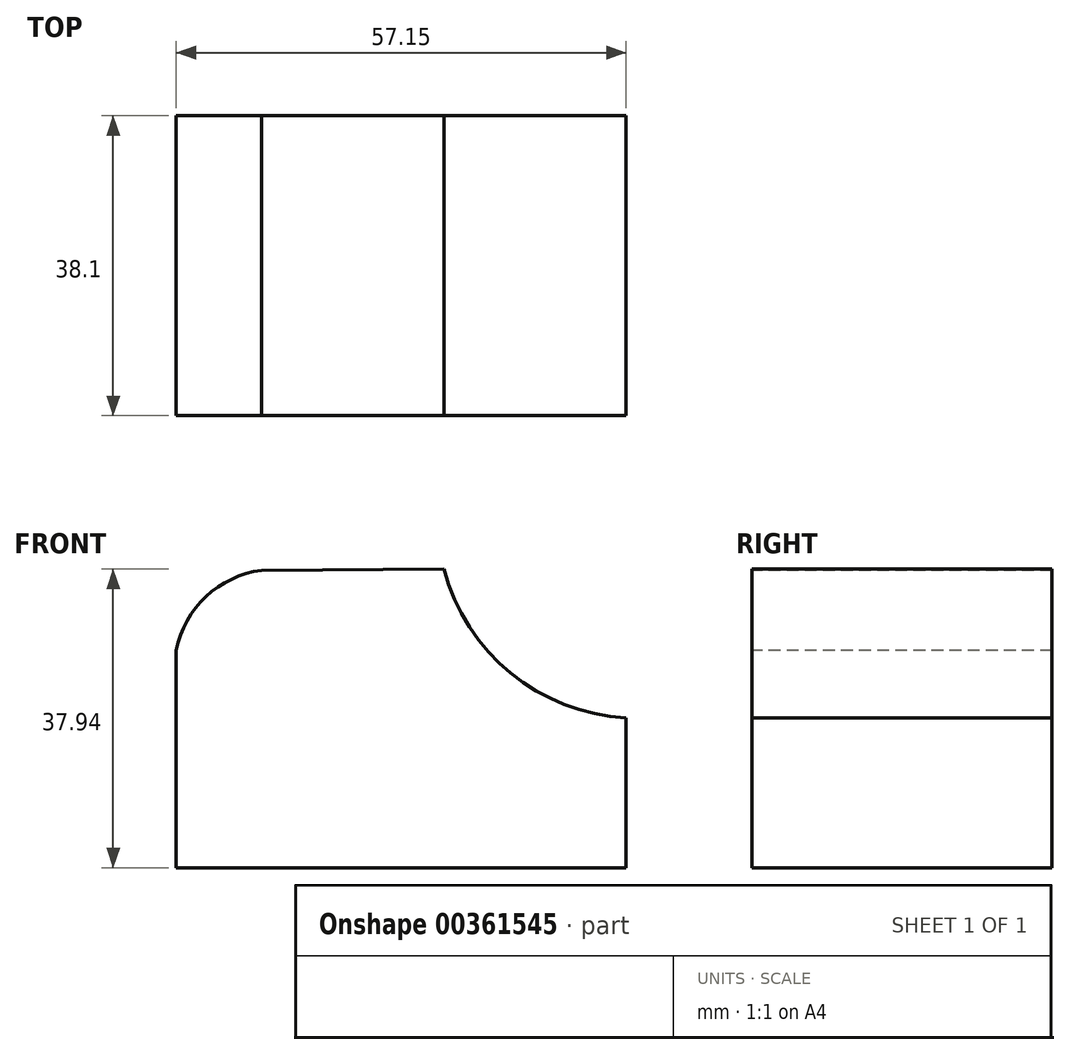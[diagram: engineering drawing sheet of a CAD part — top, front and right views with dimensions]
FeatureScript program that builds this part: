
annotation { "Feature Type Name" : "Feature", "Feature Type Description" : "" }
export const myFeature = defineFeature(function(context is Context, id is Id, definition is map)
    precondition{}
    {
        {
            var Q0;
            Q0=qCreatedBy(makeId("Front.planeOp"),FACE);
            var sketch = newSketch(context, id + "F0", { "sketchPlane" : qUnion([Q0])});
            skLineSegment(sketch, "E0", {"start": v(0, 37.71) * mm, "end": v(0, 0) * mm});
            skLineSegment(sketch, "E1", {"start": v(0, 0) * mm, "end": v(57.15, 0) * mm});
            skLineSegment(sketch, "E2", {"start": v(57.15, 0) * mm, "end": v(57.15, 38.1) * mm});
            skLineSegment(sketch, "E3", {"start": v(57.15, 38.1) * mm, "end": v(0, 37.71) * mm});
            skSolve(sketch);
        }
        {
            var Q0;
            Q0 = qSketchRegion(id + "F0", true);
            extrude(context, id + "F1", {"entities" : qUnion([Q0]), "depth" : 38.1 * mm});
        }
        {
            var Q0;
            Q0=makeQuery(id+"F1.opExtrude","CAP_FACE",FACE,{"disambiguationData":[OSD([sQuery(id+"F0.wireOp",EDGE,"E0"),sQuery(id+"F0.wireOp",EDGE,"E1"),sQuery(id+"F0.wireOp",EDGE,"E2"),sQuery(id+"F0.wireOp",EDGE,"E3")])],"isStart":false});
            var sketch = newSketch(context, id + "F2", { "sketchPlane" : qUnion([Q0])});
            skArc(sketch, "E4", {"start": v(10.83, 37.78) * mm, "mid": v(2.16, 32.61) * mm, "end": v(0, 22.75) * mm});
            skSolve(sketch);
        }
        {
            var Q0;
            {var subQ0=sQuery(id+"F2.wireOp",EDGE,"E4");var subQ1=makeQuery(id+"F1.opExtrude","CAP_EDGE",EDGE,{"disambiguationData":[OSD([sQuery(id+"F0.wireOp",EDGE,"E3")])],"isStart":false});var subQ2=makeQuery(id+"F2.imprint","INTERSECT",VERTEX,{"derivedFrom":[subQ1,subQ0]});Q0=makeQuery(id+"F2.imprint","IMPRINT",FACE,{"disambiguationData":[TD([[makeQuery(id+"F2.imprint","IMPRINT",EDGE,{"disambiguationData":[TD([[subQ2,-1.0]])],"derivedFrom":subQ0}),-1.0]])]});}
            extrude(context, id + "F3", {"entities" : qUnion([Q0]), "operationType" : NewBodyOperationType.REMOVE, "oppositeDirection" : true, "depth" : 38.1 * mm});
        }
        {
            var Q0;
            Q0=makeQuery(id+"F1.opExtrude","CAP_FACE",FACE,{"disambiguationData":[OSD([sQuery(id+"F0.wireOp",EDGE,"E0"),sQuery(id+"F0.wireOp",EDGE,"E1"),sQuery(id+"F0.wireOp",EDGE,"E2"),sQuery(id+"F0.wireOp",EDGE,"E3")])],"isStart":false});
            var sketch = newSketch(context, id + "F4", { "sketchPlane" : qUnion([Q0])});
            skArc(sketch, "E5", {"start": v(34, 37.94) * mm, "mid": v(42.5, 24.73) * mm, "end": v(57.15, 19.05) * mm});
            skSolve(sketch);
        }
        {
            var Q0;
            {var subQ0=sQuery(id+"F4.wireOp",EDGE,"E5");Q0=makeQuery(id+"F4.imprint","IMPRINT",FACE,{"disambiguationData":[TD([[makeQuery(id+"F4.imprint","IMPRINT",EDGE,{"derivedFrom":subQ0}),1.0]])]});}
            extrude(context, id + "F5", {"entities" : qUnion([Q0]), "operationType" : NewBodyOperationType.REMOVE, "oppositeDirection" : true, "depth" : 38.1 * mm});
        }
    });
